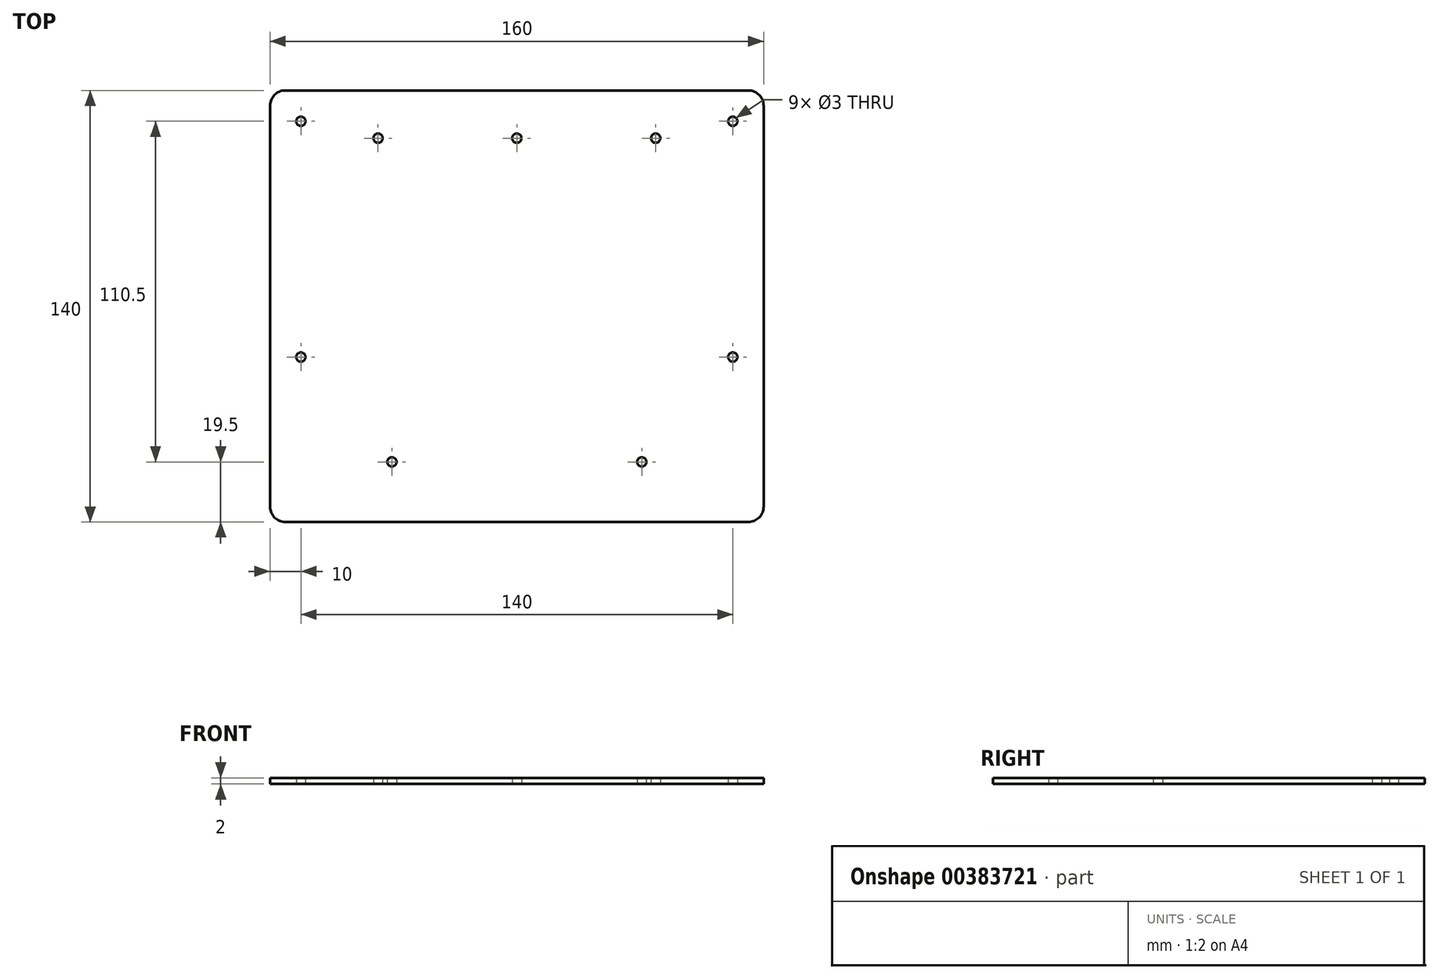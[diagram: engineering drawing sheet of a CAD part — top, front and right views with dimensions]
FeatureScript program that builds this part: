
annotation { "Feature Type Name" : "Feature", "Feature Type Description" : "" }
export const myFeature = defineFeature(function(context is Context, id is Id, definition is map)
    precondition{}
    {
        {
            var Q0;
            Q0=qCreatedBy(makeId("Top.planeOp"),FACE);
            var sketch = newSketch(context, id + "F0", { "sketchPlane" : qUnion([Q0])});
            skLineSegment(sketch, "E0.bottom", {"start": v(80, -70) * mm, "end": v(-80, -70) * mm});
            skLineSegment(sketch, "E0.top", {"start": v(80, 70) * mm, "end": v(-80, 70) * mm});
            skLineSegment(sketch, "E0.left", {"start": v(80, -70) * mm, "end": v(80, 70) * mm});
            skLineSegment(sketch, "E0.right", {"start": v(-80, -70) * mm, "end": v(-80, 70) * mm});
            skPoint(sketch, "E0.middle", {"position": v(0, 0) * mm});
            skCircle(sketch, "E1", {"center": v(-40.5, -50.5) * mm, "radius": 1.5 * mm});
            skCircle(sketch, "E2", {"center": v(40.5, -50.5) * mm, "radius": 1.5 * mm});
            skLineSegment(sketch, "E3", {"start": v(-246.7, -50.5) * mm, "end": v(233.6, -50.5) * mm, "construction": true});
            skCircle(sketch, "E4", {"center": v(-70, -16.5) * mm, "radius": 1.5 * mm});
            skCircle(sketch, "E5", {"center": v(-70, 60) * mm, "radius": 1.5 * mm});
            skCircle(sketch, "E6", {"center": v(70, 60) * mm, "radius": 1.5 * mm});
            skCircle(sketch, "E7", {"center": v(70, -16.5) * mm, "radius": 1.5 * mm});
            skLineSegment(sketch, "E8", {"start": v(-246.7, -16.5) * mm, "end": v(232.72, -16.5) * mm, "construction": true});
            skLineSegment(sketch, "E9", {"start": v(-70, 170.56) * mm, "end": v(-70, -193.48) * mm, "construction": true});
            skLineSegment(sketch, "E10", {"start": v(-243.9, 60) * mm, "end": v(231.22, 60) * mm, "construction": true});
            skLineSegment(sketch, "E11", {"start": v(70, 171.99) * mm, "end": v(70, -190.3) * mm, "construction": true});
            skLineSegment(sketch, "E12", {"start": v(-243.9, 54.5) * mm, "end": v(232.17, 54.5) * mm, "construction": true});
            skCircle(sketch, "E13", {"center": v(-45, 54.5) * mm, "radius": 1.5 * mm});
            skCircle(sketch, "E14", {"center": v(0, 54.5) * mm, "radius": 1.5 * mm});
            skCircle(sketch, "E15", {"center": v(45, 54.5) * mm, "radius": 1.5 * mm});
            skSolve(sketch);
        }
        {
            var Q0;
            Q0 = qSketchRegion(id + "F0", true);
            extrude(context, id + "F1", {"entities" : qUnion([Q0]), "depth" : 2 * mm});
        }
        {
            var Q0;
            Q0=makeQuery(id+"F1.opExtrude","SWEPT_EDGE",EDGE,{"disambiguationData":[OSD([sQuery(id+"F0.wireOp",EDGE,"E0.bottom"),sQuery(id+"F0.wireOp",EDGE,"E0.left")])]});
            var Q1;
            Q1=makeQuery(id+"F1.opExtrude","SWEPT_EDGE",EDGE,{"disambiguationData":[OSD([sQuery(id+"F0.wireOp",EDGE,"E0.bottom"),sQuery(id+"F0.wireOp",EDGE,"E0.right")])]});
            var Q2;
            Q2=makeQuery(id+"F1.opExtrude","SWEPT_EDGE",EDGE,{"disambiguationData":[OSD([sQuery(id+"F0.wireOp",EDGE,"E0.top"),sQuery(id+"F0.wireOp",EDGE,"E0.right")])]});
            var Q3;
            Q3=makeQuery(id+"F1.opExtrude","SWEPT_EDGE",EDGE,{"disambiguationData":[OSD([sQuery(id+"F0.wireOp",EDGE,"E0.top"),sQuery(id+"F0.wireOp",EDGE,"E0.left")])]});
            fillet(context, id + "F2", {"entities" : qUnion([Q0, Q1, Q2, Q3]), "radius" : 5 * mm, "tangentPropagation" : true, "allowEdgeOverflow" : false});
        }
    });
